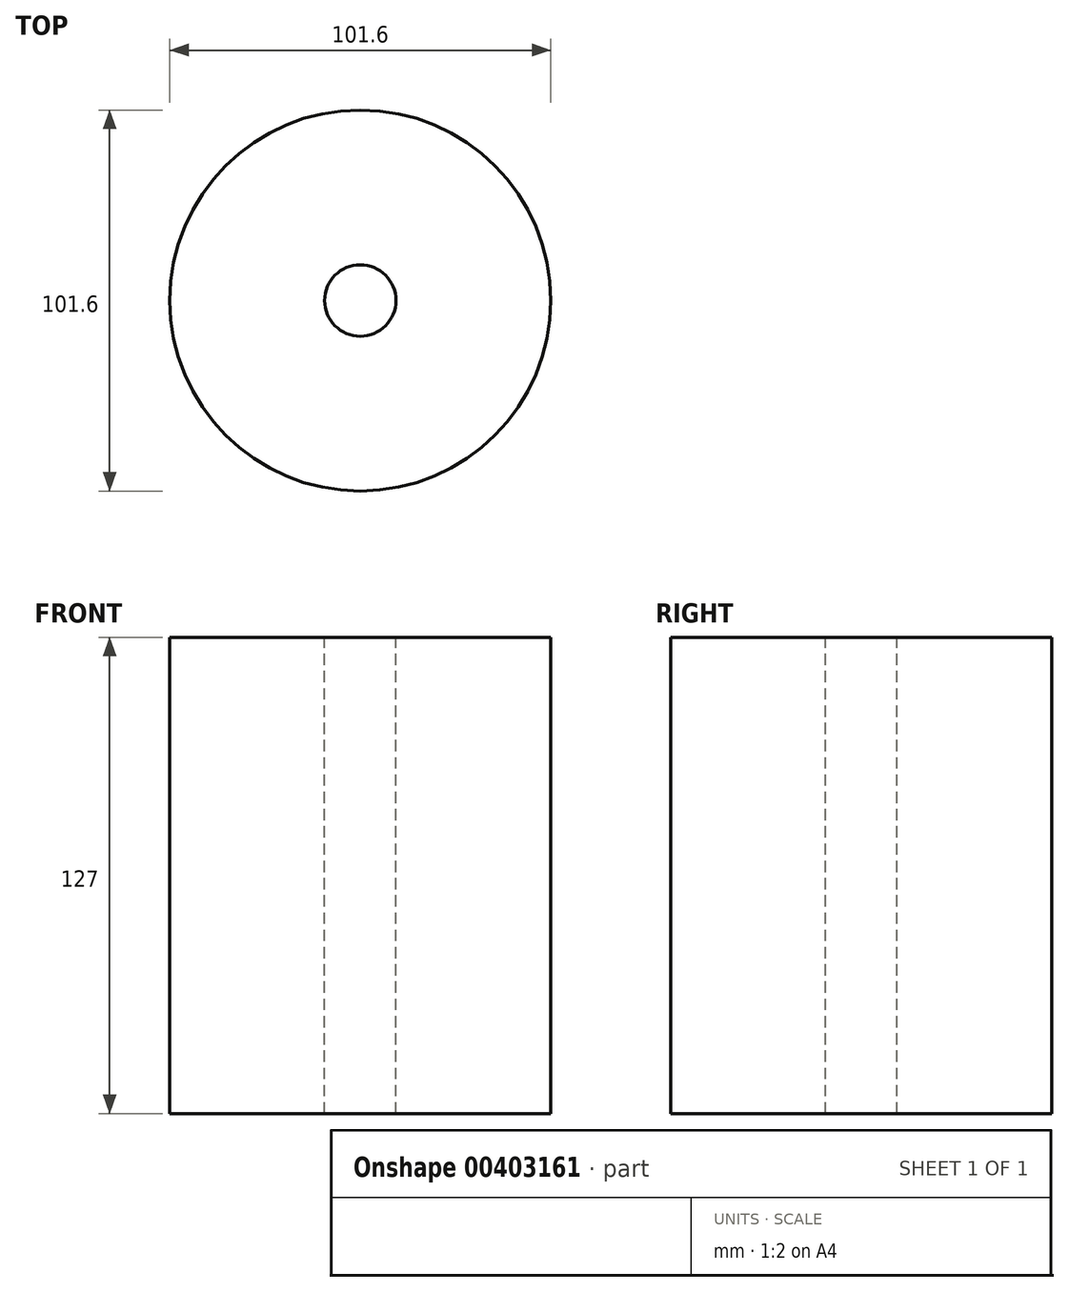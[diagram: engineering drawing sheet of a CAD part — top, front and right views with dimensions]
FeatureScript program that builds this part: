
annotation { "Feature Type Name" : "Feature", "Feature Type Description" : "" }
export const myFeature = defineFeature(function(context is Context, id is Id, definition is map)
    precondition{}
    {
        {
            var Q0;
            Q0=qCreatedBy(makeId("Top.planeOp"),FACE);
            var sketch = newSketch(context, id + "F0", { "sketchPlane" : qUnion([Q0])});
            skCircle(sketch, "E0", {"center": v(0, 0) * mm, "radius": 50.8 * mm});
            skSolve(sketch);
        }
        {
            var Q0;
            Q0 = qSketchRegion(id + "F0", true);
            var Q1;
            Q1=makeQuery(id+"F0.imprint","IMPRINT",FACE,{"disambiguationData":[TD([[makeQuery(id+"F0.imprint","IMPRINT",EDGE,{"derivedFrom":sQuery(id+"F0.wireOp",EDGE,"E0")}),1.0]])]});
            extrude(context, id + "F1", {"entities" : qUnion([Q0, Q1]), "endBound" : BoundingType.SYMMETRIC, "depth" : 127 * mm});
        }
        {
            var Q0;
            Q0=sQuery(id+"F0.wireOp",VERTEX,"E0.center");
            var Q1;
            Q1=makeQuery(id+"F1.opExtrude","SWEPT_BODY",BODY,{"disambiguationData":[OSD([sQuery(id+"F0.wireOp",EDGE,"E0")])]});
            hole(context, id + "F2", {"style" : HoleStyle.SIMPLE, "endStyle" : HoleEndStyle.THROUGH, "holeDiameter" : 19.05 * mm, "isTappedThrough" : true, "tappedDepth" : 12.7 * mm, "tapClearance" : 3, "locations" : qUnion([Q0]), "scope" : qUnion([Q1])});
        }
        {
            var Q0;
            Q0=sQuery(id+"F0.wireOp",VERTEX,"E0.center");
            var Q1;
            Q1=makeQuery(id+"F1.opExtrude","SWEPT_BODY",BODY,{"disambiguationData":[OSD([sQuery(id+"F0.wireOp",EDGE,"E0")])]});
            hole(context, id + "F3", {"style" : HoleStyle.SIMPLE, "endStyle" : HoleEndStyle.THROUGH, "oppositeDirection" : true, "holeDiameter" : 19.05 * mm, "isTappedThrough" : true, "tappedDepth" : 12.7 * mm, "tapClearance" : 3, "locations" : qUnion([Q0]), "scope" : qUnion([Q1])});
        }
    });
